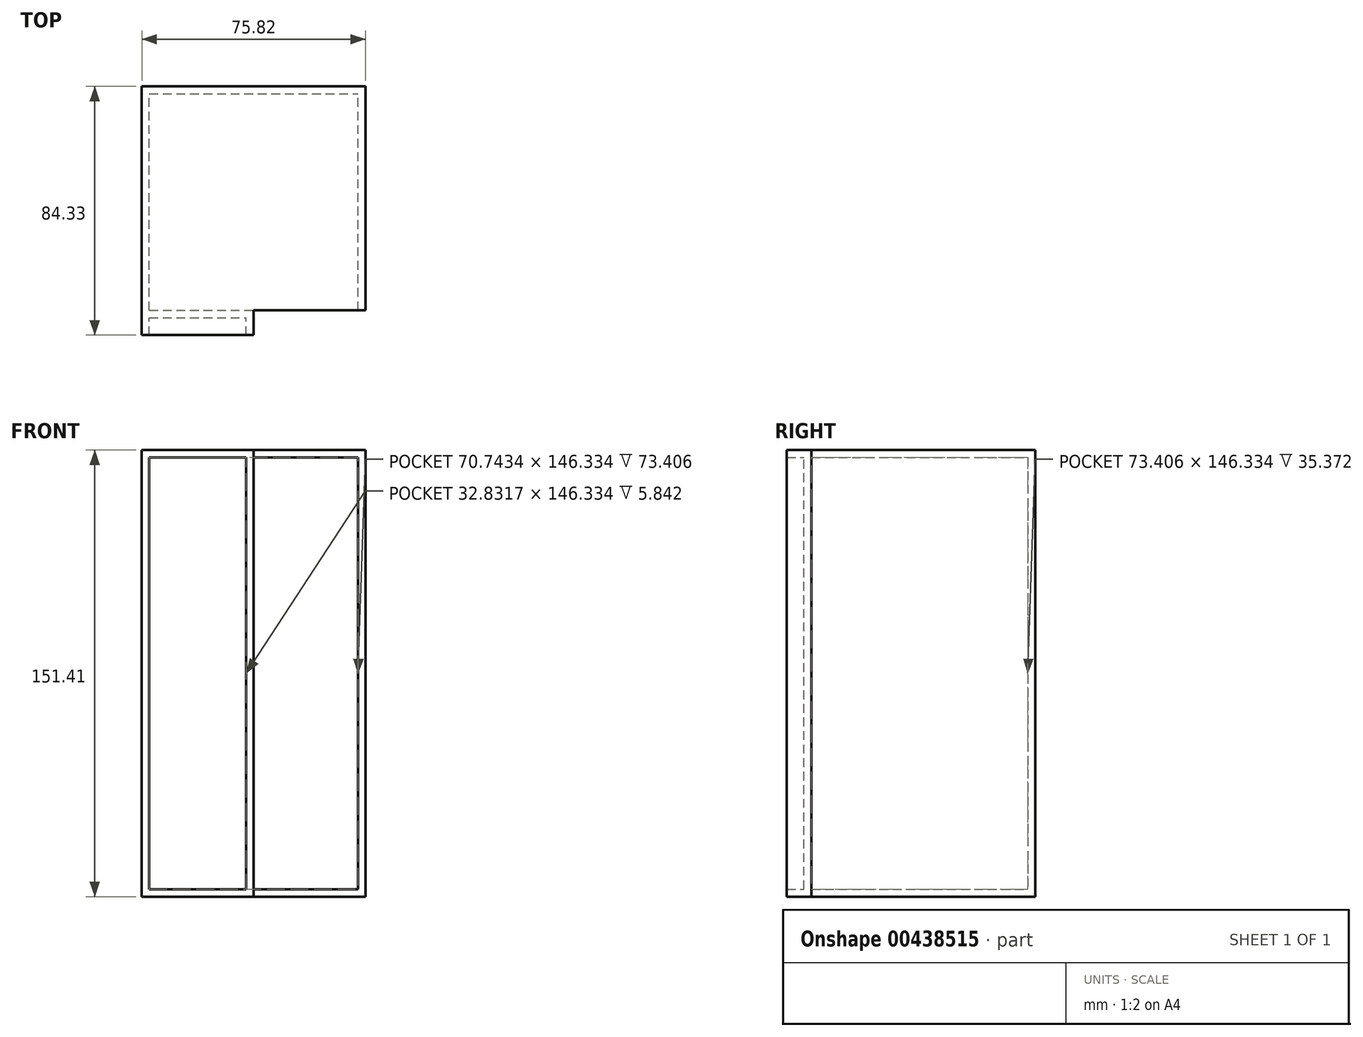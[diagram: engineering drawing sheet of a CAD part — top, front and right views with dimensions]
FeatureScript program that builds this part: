
annotation { "Feature Type Name" : "Feature", "Feature Type Description" : "" }
export const myFeature = defineFeature(function(context is Context, id is Id, definition is map)
    precondition{}
    {
        {
            var Q0;
            Q0=qCreatedBy(makeId("Front.planeOp"),FACE);
            var sketch = newSketch(context, id + "F0", { "sketchPlane" : qUnion([Q0])});
            skLineSegment(sketch, "E0.bottom", {"start": v(-75.82, 75.6) * mm, "end": v(0, 75.6) * mm});
            skLineSegment(sketch, "E0.top", {"start": v(-75.82, -75.82) * mm, "end": v(0, -75.82) * mm});
            skLineSegment(sketch, "E0.left", {"start": v(-75.82, 75.6) * mm, "end": v(-75.82, -75.82) * mm});
            skLineSegment(sketch, "E0.right", {"start": v(0, 75.6) * mm, "end": v(0, -75.82) * mm});
            skSolve(sketch);
        }
        {
            var Q0;
            Q0=makeQuery(id+"F0.imprint","IMPRINT",FACE,{"disambiguationData":[TD([[makeQuery(id+"F0.imprint","IMPRINT",EDGE,{"derivedFrom":sQuery(id+"F0.wireOp",EDGE,"E0.bottom")}),-1.0]])]});
            extrude(context, id + "F1", {"entities" : qUnion([Q0]), "depth" : 75.95 * mm});
        }
        {
            var Q0;
            Q0=makeQuery(id+"F1.opExtrude","CAP_FACE",FACE,{"disambiguationData":[OSD([sQuery(id+"F0.wireOp",EDGE,"E0.bottom"),sQuery(id+"F0.wireOp",EDGE,"E0.top"),sQuery(id+"F0.wireOp",EDGE,"E0.left"),sQuery(id+"F0.wireOp",EDGE,"E0.right")])],"isStart":false});
            var sketch = newSketch(context, id + "F2", { "sketchPlane" : qUnion([Q0])});
            skLineSegment(sketch, "E1", {"start": v(-37.91, 75.6) * mm, "end": v(-37.91, -75.82) * mm});
            skSolve(sketch);
        }
        {
            var Q0;
            Q0=makeQuery(id+"F1.opExtrude","CAP_FACE",FACE,{"disambiguationData":[OSD([sQuery(id+"F0.wireOp",EDGE,"E0.bottom"),sQuery(id+"F0.wireOp",EDGE,"E0.top"),sQuery(id+"F0.wireOp",EDGE,"E0.left"),sQuery(id+"F0.wireOp",EDGE,"E0.right")])],"isStart":false});
            shell(context, id + "F3", {"entities" : qUnion([Q0]), "thickness" : 2.54 * mm});
        }
        {
            var Q0;
            {var subQ0=sQuery(id+"F2.wireOp",EDGE,"E1");Q0=makeQuery(id+"F2.imprint","IMPRINT",FACE,{"disambiguationData":[TD([[makeQuery(id+"F2.imprint","IMPRINT",EDGE,{"derivedFrom":subQ0}),-1.0]])]});}
            extrude(context, id + "F4", {"entities" : qUnion([Q0]), "operationType" : NewBodyOperationType.ADD, "depth" : 8.38 * mm});
        }
        {
            var Q0;
            Q0=makeQuery(id+"F4.opExtrude","CAP_FACE",FACE,{"disambiguationData":[OSD([sQuery(id+"F0.wireOp",EDGE,"E0.bottom"),sQuery(id+"F0.wireOp",EDGE,"E0.top"),sQuery(id+"F0.wireOp",EDGE,"E0.left"),sQuery(id+"F2.wireOp",EDGE,"E1")])],"isStart":false});
            shell(context, id + "F5", {"entities" : qUnion([Q0]), "thickness" : 2.54 * mm});
        }
    });
